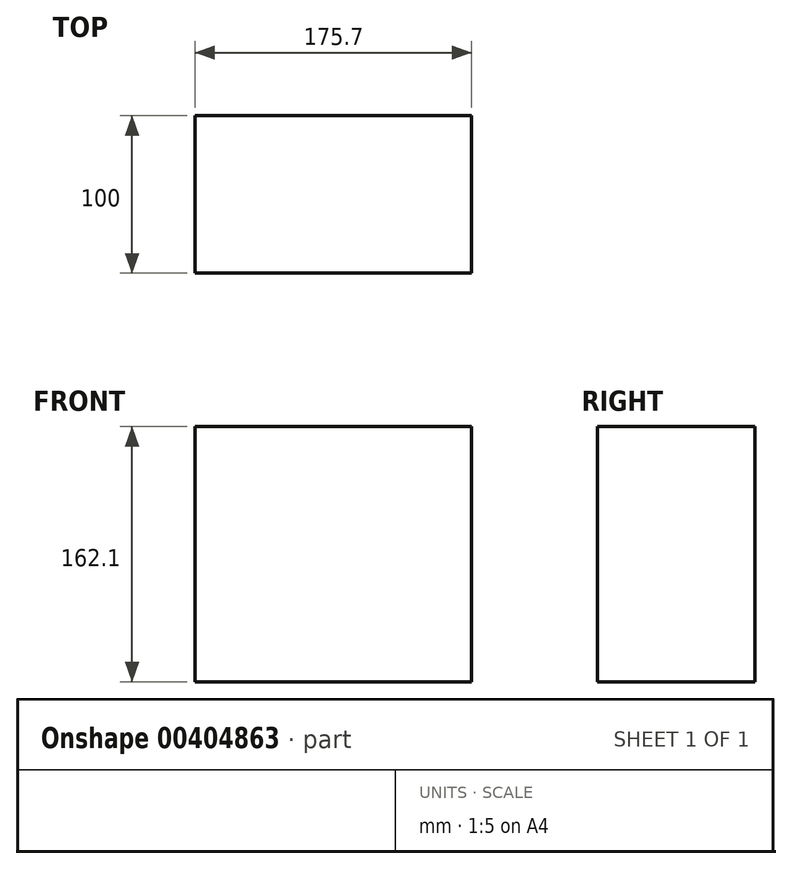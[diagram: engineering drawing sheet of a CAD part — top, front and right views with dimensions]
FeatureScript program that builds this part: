
annotation { "Feature Type Name" : "Feature", "Feature Type Description" : "" }
export const myFeature = defineFeature(function(context is Context, id is Id, definition is map)
    precondition{}
    {
        {
            var Q0;
            Q0=qCreatedBy(makeId("Front.planeOp"),FACE);
            var sketch = newSketch(context, id + "F0", { "sketchPlane" : qUnion([Q0])});
            skLineSegment(sketch, "E0.bottom", {"start": v(-89.33, 77.47) * mm, "end": v(86.37, 77.47) * mm});
            skLineSegment(sketch, "E0.top", {"start": v(-89.33, -84.63) * mm, "end": v(86.37, -84.63) * mm});
            skLineSegment(sketch, "E0.left", {"start": v(-89.33, 77.47) * mm, "end": v(-89.33, -84.63) * mm});
            skLineSegment(sketch, "E0.right", {"start": v(86.37, 77.47) * mm, "end": v(86.37, -84.63) * mm});
            skSolve(sketch);
        }
        {
            var Q0;
            Q0 = qSketchRegion(id + "F2", true);
            var Q1;
            Q1 = qSketchRegion(id + "F0", true);
            var Q2;
            Q2 = qSketchRegion(id + "F2", true);
            var Q3;
            Q3 = qSketchRegion(id + "F2", true);
            extrude(context, id + "F1", {"entities" : qUnion([Q0, Q1, Q2, Q3]), "oppositeDirection" : true, "depth" : 100 * mm});
        }
    });
